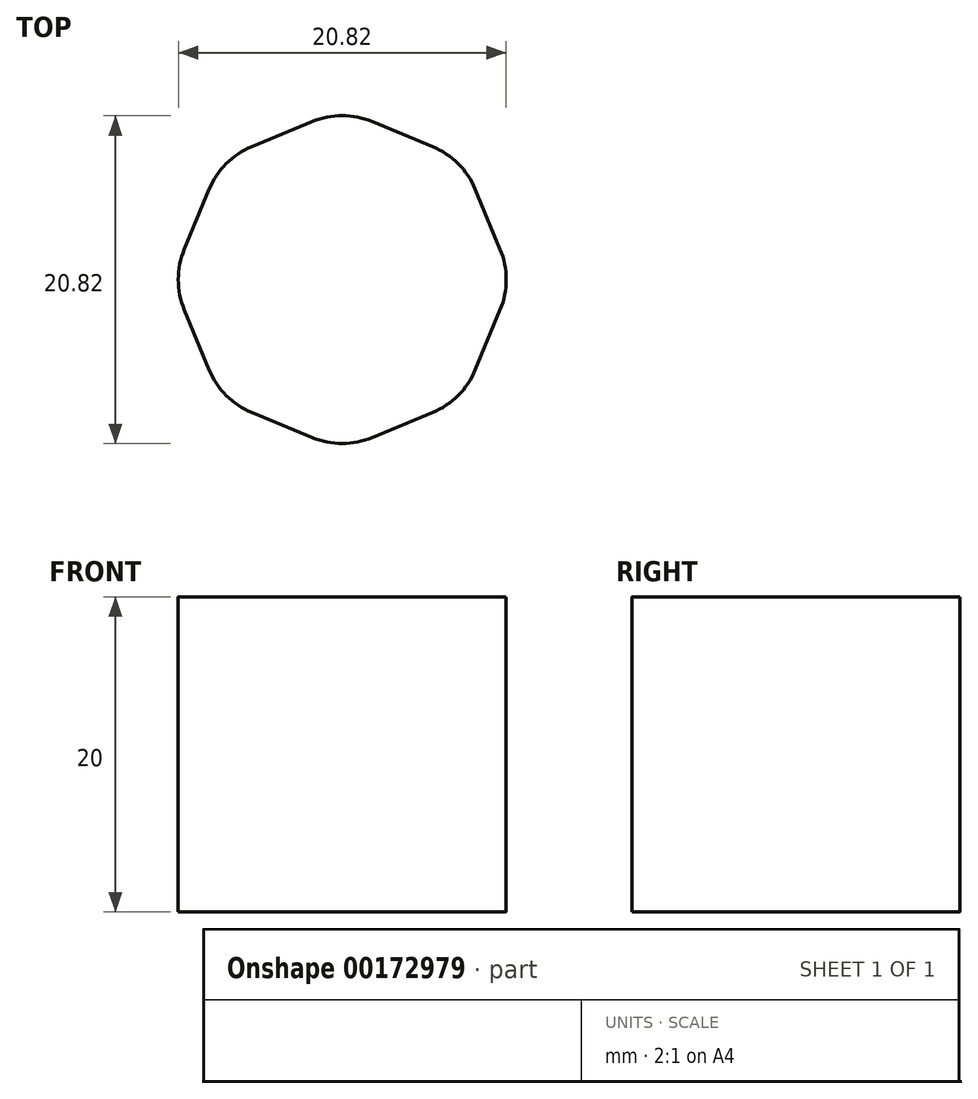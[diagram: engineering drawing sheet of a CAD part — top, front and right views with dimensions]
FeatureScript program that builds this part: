
annotation { "Feature Type Name" : "Feature", "Feature Type Description" : "" }
export const myFeature = defineFeature(function(context is Context, id is Id, definition is map)
    precondition{}
    {
        {
            var Q0;
            Q0=qCreatedBy(makeId("Top.planeOp"),FACE);
            var sketch = newSketch(context, id + "F0", { "sketchPlane" : qUnion([Q0])});
            skCircle(sketch, "E0.cCircle", {"center": v(0, 0) * mm, "radius": 10 * mm, "construction": true});
            skLineSegment(sketch, "E0.0", {"start": v(-10.82, 0) * mm, "end": v(-7.65, 7.65) * mm});
            skLineSegment(sketch, "E0.1", {"start": v(-7.65, 7.65) * mm, "end": v(0, 10.82) * mm});
            skLineSegment(sketch, "E0.2", {"start": v(0, 10.82) * mm, "end": v(7.65, 7.65) * mm});
            skLineSegment(sketch, "E0.3", {"start": v(7.65, 7.65) * mm, "end": v(10.82, 0) * mm});
            skLineSegment(sketch, "E0.4", {"start": v(10.82, 0) * mm, "end": v(7.65, -7.65) * mm});
            skLineSegment(sketch, "E0.5", {"start": v(7.65, -7.65) * mm, "end": v(0, -10.82) * mm});
            skLineSegment(sketch, "E0.6", {"start": v(0, -10.82) * mm, "end": v(-7.65, -7.65) * mm});
            skLineSegment(sketch, "E0.7", {"start": v(-7.65, -7.65) * mm, "end": v(-10.82, 0) * mm});
            skPoint(sketch, "E0.0.midPoint", {"position": v(-9.24, 3.83) * mm});
            skSolve(sketch);
        }
        {
            var Q0;
            Q0=makeQuery(id+"F0.imprint","IMPRINT",FACE,{"disambiguationData":[TD([[makeQuery(id+"F0.imprint","IMPRINT",EDGE,{"derivedFrom":sQuery(id+"F0.wireOp",EDGE,"E0.0")}),-1.0]])]});
            extrude(context, id + "F1", {"entities" : qUnion([Q0]), "depth" : 20 * mm});
        }
        {
            var Q0;
            Q0=makeQuery(id+"F1.opExtrude","SWEPT_EDGE",EDGE,{"disambiguationData":[OSD([sQuery(id+"F0.wireOp",EDGE,"E0.5"),sQuery(id+"F0.wireOp",EDGE,"E0.6")])]});
            var Q1;
            Q1=makeQuery(id+"F1.opExtrude","SWEPT_EDGE",EDGE,{"disambiguationData":[OSD([sQuery(id+"F0.wireOp",EDGE,"E0.4"),sQuery(id+"F0.wireOp",EDGE,"E0.5")])]});
            var Q2;
            Q2=makeQuery(id+"F1.opExtrude","SWEPT_EDGE",EDGE,{"disambiguationData":[OSD([sQuery(id+"F0.wireOp",EDGE,"E0.3"),sQuery(id+"F0.wireOp",EDGE,"E0.4")])]});
            var Q3;
            Q3=makeQuery(id+"F1.opExtrude","SWEPT_EDGE",EDGE,{"disambiguationData":[OSD([sQuery(id+"F0.wireOp",EDGE,"E0.2"),sQuery(id+"F0.wireOp",EDGE,"E0.3")])]});
            var Q4;
            Q4=makeQuery(id+"F1.opExtrude","SWEPT_EDGE",EDGE,{"disambiguationData":[OSD([sQuery(id+"F0.wireOp",EDGE,"E0.1"),sQuery(id+"F0.wireOp",EDGE,"E0.2")])]});
            var Q5;
            Q5=makeQuery(id+"F1.opExtrude","SWEPT_EDGE",EDGE,{"disambiguationData":[OSD([sQuery(id+"F0.wireOp",EDGE,"E0.0"),sQuery(id+"F0.wireOp",EDGE,"E0.1")])]});
            var Q6;
            Q6=makeQuery(id+"F1.opExtrude","SWEPT_EDGE",EDGE,{"disambiguationData":[OSD([sQuery(id+"F0.wireOp",EDGE,"E0.0"),sQuery(id+"F0.wireOp",EDGE,"E0.7")])]});
            var Q7;
            Q7=makeQuery(id+"F1.opExtrude","SWEPT_EDGE",EDGE,{"disambiguationData":[OSD([sQuery(id+"F0.wireOp",EDGE,"E0.6"),sQuery(id+"F0.wireOp",EDGE,"E0.7")])]});
            fillet(context, id + "F2", {"entities" : qUnion([Q0, Q1, Q2, Q3, Q4, Q5, Q6, Q7]), "radius" : 5 * mm, "tangentPropagation" : true, "allowEdgeOverflow" : false});
        }
    });
